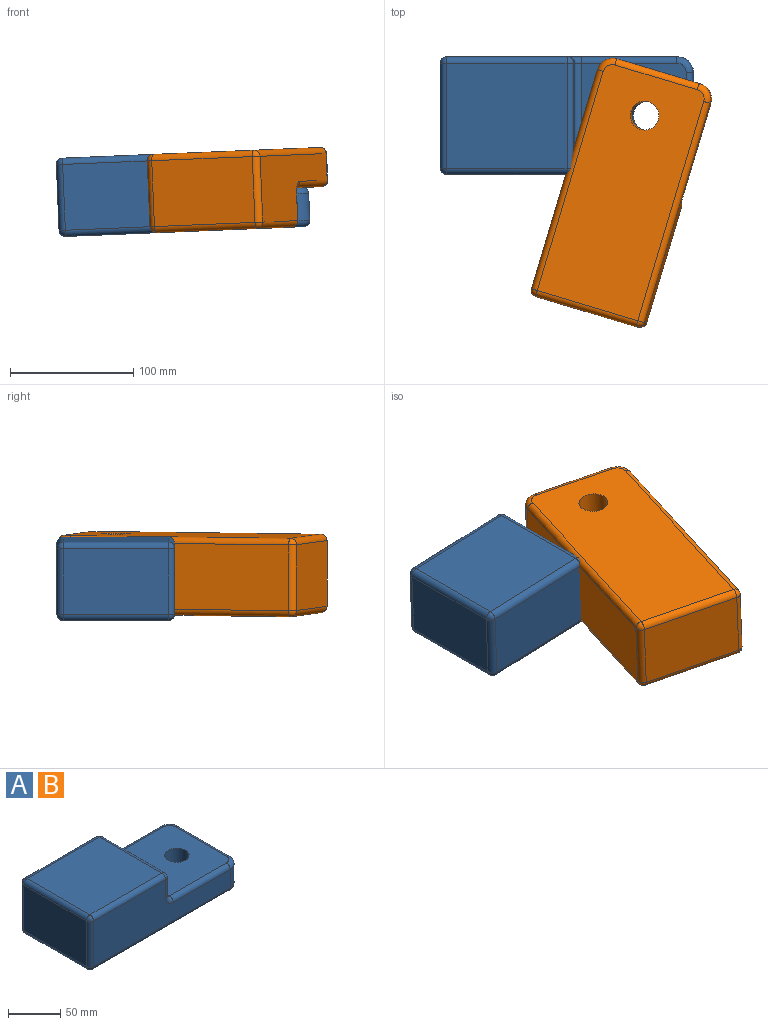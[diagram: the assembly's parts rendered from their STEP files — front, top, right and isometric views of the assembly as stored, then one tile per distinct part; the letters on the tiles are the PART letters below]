
ASSEMBLY  parts=2 mates=1
PART A: 39 faces, bbox 204.2x97.3x63.5 mm
  f0: plane 85.09x21.59mm, normal (1,0,0), area 1837.1mm2, adj f17,f18,f21,f22
  f1: plane 185.42x53.34mm, normal (0,1,0), area 7130.2mm2, adj f8,f16,f19,f21,f26,f33,f38
  f2: plane 85.09x53.34mm, normal (-1,0,0), area 4538.7mm2, adj f27,f28,f33,f34
  f3: plane 185.42x53.34mm, normal (0,-1,0), area 7130.2mm2, adj f6,f13,f15,f18,f23,f28,f29
  f4: plane 97.79x85.09mm, normal (0,0,1), area 8321mm2, adj f22,f23,f26,f27
  f5: plane 193.04x85.09mm, normal (0,0,-1), area 15973mm2, adj f9,f29,f32,f34,f35,f37,f38
  f6: cylinder r=12.7mm len=21.59mm, axis (0,0,-1), area 430.7mm2, adj f3,f7,f11,f32
  f7: plane 69.85x21.59mm, normal (1,0,0), area 1508.1mm2, adj f6,f8,f12,f35
  f8: cylinder r=12.7mm len=21.59mm, axis (0,0,-1), area 430.7mm2, adj f1,f7,f14,f37
  f9: cylinder r=11.67mm len=31.75mm, axis (0,0,-1), area 2328mm2, adj f5,f10
  f10: plane 85.09x85.09mm, normal (0,0,1), area 6787.5mm2, adj f9,f11,f12,f13,f14,f16,f17
  f11: torus R=7.62mm, axis (0,0,1), area 136mm2, adj f6,f10,f12,f13
  f12: cylinder r=5.08mm len=69.85mm, axis (0,-1,0), area 557.4mm2, adj f7,f10,f11,f14
  f13: cylinder r=5.08mm len=77.47mm, axis (-1,0,0), area 618.2mm2, adj f3,f10,f11,f15
  f14: torus R=7.62mm, axis (0,0,1), area 136mm2, adj f8,f10,f12,f16
  f15: torus R=10.16mm, axis (0,1,0), area 86.8mm2, adj f3,f13,f17,f18
  f16: cylinder r=5.08mm len=77.47mm, axis (1,0,0), area 618.2mm2, adj f1,f10,f14,f19
  f17: cylinder r=5.08mm len=85.09mm, axis (0,1,0), area 679mm2, adj f0,f10,f15,f19
  f18: cylinder r=5.08mm len=21.59mm, axis (0,0,1), area 172.3mm2, adj f0,f3,f15,f20
  f19: torus R=10.16mm, axis (0,1,0), area 86.8mm2, adj f1,f16,f17,f21
  f20: sphere r=5.08mm, area 40.5mm2, adj f18,f22,f23
  f21: cylinder r=5.08mm len=21.59mm, axis (0,0,-1), area 172.3mm2, adj f0,f1,f19,f24
  f22: cylinder r=5.08mm len=85.09mm, axis (0,-1,0), area 679mm2, adj f0,f4,f20,f24
  f23: cylinder r=5.08mm len=97.79mm, axis (-1,0,0), area 780.3mm2, adj f3,f4,f20,f25
  f24: sphere r=5.08mm, area 40.5mm2, adj f21,f22,f26
  f25: sphere r=5.08mm, area 40.5mm2, adj f23,f27,f28
  f26: cylinder r=5.08mm len=97.79mm, axis (1,0,0), area 780.3mm2, adj f1,f4,f24,f30
  f27: cylinder r=5.08mm len=85.09mm, axis (0,1,0), area 679mm2, adj f2,f4,f25,f30
  f28: cylinder r=5.08mm len=53.34mm, axis (0,0,-1), area 425.6mm2, adj f2,f3,f25,f31
  f29: cylinder r=5.08mm len=185.42mm, axis (1,0,0), area 1479.6mm2, adj f3,f5,f31,f32
  f30: sphere r=5.08mm, area 40.5mm2, adj f26,f27,f33
  f31: sphere r=5.08mm, area 40.5mm2, adj f28,f29,f34
  f32: torus R=7.62mm, axis (0,0,1), area 136mm2, adj f5,f6,f29,f35
  f33: cylinder r=5.08mm len=53.34mm, axis (0,0,1), area 425.6mm2, adj f1,f2,f30,f36
  f34: cylinder r=5.08mm len=85.09mm, axis (0,-1,0), area 679mm2, adj f2,f5,f31,f36
  f35: cylinder r=5.08mm len=69.85mm, axis (0,1,0), area 557.4mm2, adj f5,f7,f32,f37
  f36: sphere r=5.08mm, area 40.5mm2, adj f33,f34,f38
  f37: torus R=7.62mm, axis (0,0,1), area 136mm2, adj f5,f8,f35,f38
  f38: cylinder r=5.08mm len=185.42mm, axis (-1,0,0), area 1479.6mm2, adj f1,f5,f36,f37
PART B: same geometry as A
PLACE A rot(axis=(0,-1,0),2.4deg) t=(30.34,127.58,25.38)mm fixed
PLACE B rot(axis=(0.8,0.6,0.02),178.6deg) t=(-44.5,224.78,85.84)mm
MATE revolute A.f9 <-> B.f9  axis (-0.04,0,1) through (-8.39,175.21,55.56)mm
